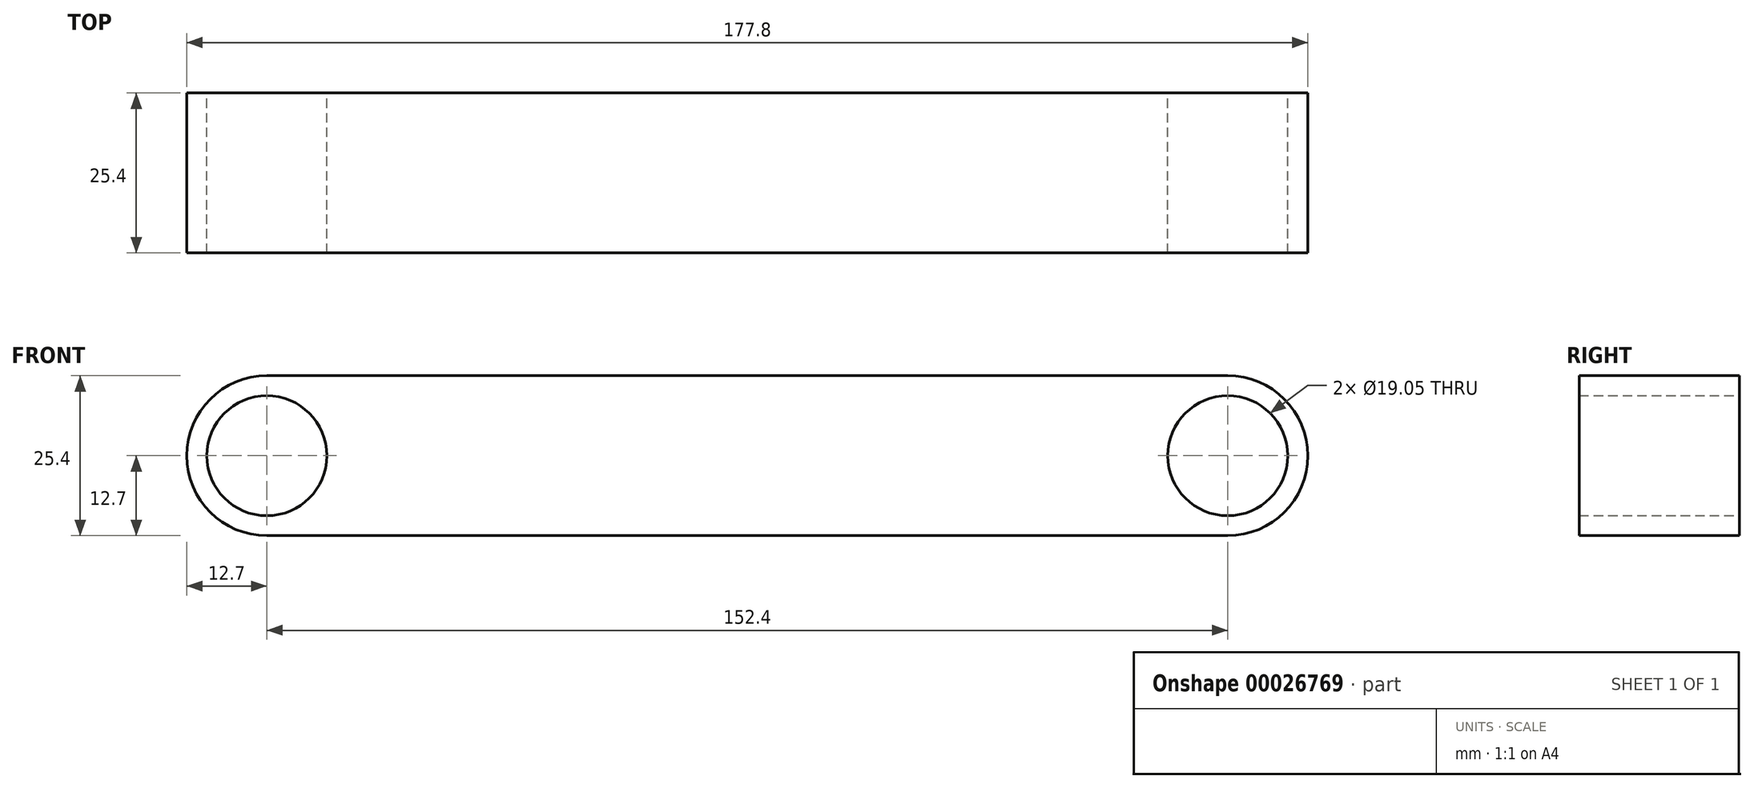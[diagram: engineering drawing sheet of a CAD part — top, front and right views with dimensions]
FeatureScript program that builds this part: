
annotation { "Feature Type Name" : "Feature", "Feature Type Description" : "" }
export const myFeature = defineFeature(function(context is Context, id is Id, definition is map)
    precondition{}
    {
        {
            var Q0;
            Q0=qCreatedBy(makeId("Front.planeOp"),FACE);
            var sketch = newSketch(context, id + "F0", { "sketchPlane" : qUnion([Q0])});
            skArc(sketch, "E0", {"start": v(-69.63, 12.7) * mm, "mid": v(-82.33, 0) * mm, "end": v(-69.63, -12.7) * mm});
            skArc(sketch, "E1", {"start": v(82.77, -12.7) * mm, "mid": v(95.47, 0) * mm, "end": v(82.77, 12.7) * mm});
            skPoint(sketch, "E2", {"position": v(-69.63, 12.7) * mm});
            skPoint(sketch, "E3", {"position": v(-69.63, -12.7) * mm});
            skPoint(sketch, "E4", {"position": v(82.77, 12.7) * mm});
            skPoint(sketch, "E5", {"position": v(82.77, -12.7) * mm});
            skLineSegment(sketch, "E6", {"start": v(-69.63, 12.7) * mm, "end": v(82.77, 12.7) * mm});
            skLineSegment(sketch, "E7", {"start": v(-69.63, -12.7) * mm, "end": v(82.77, -12.7) * mm});
            skCircle(sketch, "E8", {"center": v(-69.63, 0) * mm, "radius": 9.53 * mm});
            skCircle(sketch, "E9", {"center": v(82.77, 0) * mm, "radius": 9.53 * mm});
            skSolve(sketch);
        }
        {
            var Q0;
            Q0 = qSketchRegion(id + "F0", true);
            extrude(context, id + "F1", {"entities" : qUnion([Q0]), "depth" : 25.4 * mm});
        }
    });
